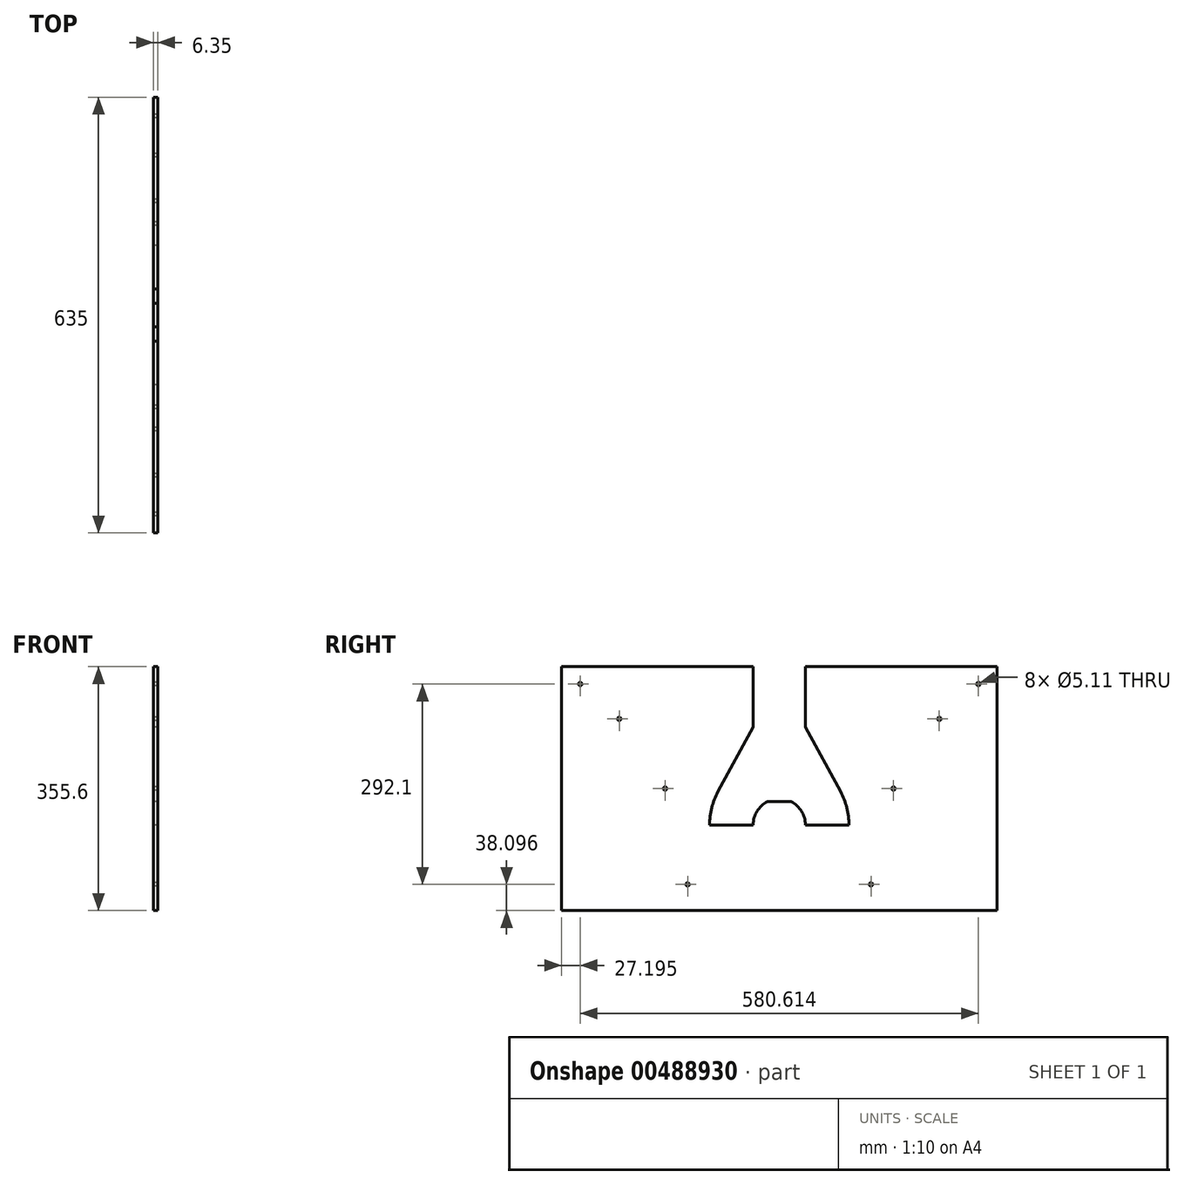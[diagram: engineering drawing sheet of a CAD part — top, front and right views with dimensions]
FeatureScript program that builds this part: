
annotation { "Feature Type Name" : "Feature", "Feature Type Description" : "" }
export const myFeature = defineFeature(function(context is Context, id is Id, definition is map)
    precondition{}
    {
        {
            var Q0;
            Q0=qCreatedBy(makeId("Right.planeOp"),FACE);
            var sketch = newSketch(context, id + "F0", { "sketchPlane" : qUnion([Q0])});
            skLineSegment(sketch, "E0.0", {"start": v(127.66, -203.13) * mm, "end": v(127.66, -196.78) * mm, "construction": true});
            skLineSegment(sketch, "E1.0", {"start": v(-507.34, -152.33) * mm, "end": v(-507.34, -145.98) * mm, "construction": true});
            skLineSegment(sketch, "E2.bottom", {"start": v(-507.34, -152.33) * mm, "end": v(127.66, -152.33) * mm});
            skLineSegment(sketch, "E2.top", {"start": v(-507.34, 203.27) * mm, "end": v(-227.94, 203.27) * mm});
            skLineSegment(sketch, "E2.left", {"start": v(-507.34, -152.33) * mm, "end": v(-507.34, 203.27) * mm});
            skLineSegment(sketch, "E2.right", {"start": v(127.66, -152.33) * mm, "end": v(127.66, 203.27) * mm});
            skLineSegment(sketch, "E3", {"start": v(-189.84, 203.27) * mm, "end": v(-189.84, -152.33) * mm, "construction": true});
            skPoint(sketch, "E4", {"position": v(-42.52, -6.28) * mm});
            skArc(sketch, "E5", {"start": v(127.66, 203.27) * mm, "mid": v(-17.26, 52.16) * mm, "end": v(-62.2, -152.33) * mm, "construction": true});
            skArc(sketch, "E6.0", {"start": v(127.66, 195.88) * mm, "mid": v(-9.58, 53) * mm, "end": v(-56.37, -139.5) * mm, "construction": true});
            skArc(sketch, "E7.0", {"start": v(99.66, 185.1) * mm, "mid": v(-22, 42.97) * mm, "end": v(-62.72, -139.65) * mm, "construction": true});
            skCircle(sketch, "E8", {"center": v(-56.16, -114.23) * mm, "radius": 2.55 * mm});
            skCircle(sketch, "E9", {"center": v(-23.27, 25.47) * mm, "radius": 2.55 * mm});
            skCircle(sketch, "E10", {"center": v(43.51, 127.07) * mm, "radius": 2.55 * mm});
            skCircle(sketch, "E11.MirrorC", {"center": v(-423.19, 127.07) * mm, "radius": 2.55 * mm});
            skCircle(sketch, "E12.MirrorC", {"center": v(-356.4, 25.47) * mm, "radius": 2.55 * mm});
            skCircle(sketch, "E13.MirrorC", {"center": v(-323.51, -114.23) * mm, "radius": 2.55 * mm});
            skLineSegment(sketch, "E14", {"start": v(-227.94, 6.42) * mm, "end": v(-151.74, 6.42) * mm});
            skLineSegment(sketch, "E15", {"start": v(-151.74, 114.93) * mm, "end": v(-151.74, 203.27) * mm});
            skLineSegment(sketch, "E16", {"start": v(-227.94, 114.93) * mm, "end": v(-227.94, 203.27) * mm});
            skPoint(sketch, "E17", {"position": v(-189.84, 6.42) * mm});
            skCircle(sketch, "E18", {"center": v(100.47, 177.87) * mm, "radius": 2.55 * mm});
            skCircle(sketch, "E19.MirrorC", {"center": v(-480.15, 177.87) * mm, "radius": 2.55 * mm});
            skLineSegment(sketch, "E20.trimOffspring", {"start": v(-151.74, 203.27) * mm, "end": v(127.66, 203.27) * mm});
            skArc(sketch, "E21", {"start": v(-88.24, -27.56) * mm, "mid": v(-91.38, -2.5) * mm, "end": v(-100.6, 21.02) * mm});
            skLineSegment(sketch, "E22", {"start": v(-291.44, -27.56) * mm, "end": v(-227.94, -27.56) * mm});
            skPoint(sketch, "E23.orphan", {"position": v(-310.29, -27.56) * mm});
            skArc(sketch, "E24", {"start": v(-151.74, -27.56) * mm, "mid": v(-189.84, 10.54) * mm, "end": v(-227.94, -27.56) * mm});
            skLineSegment(sketch, "E25.trimOffspring", {"start": v(-151.74, -27.56) * mm, "end": v(-88.24, -27.56) * mm});
            skLineSegment(sketch, "E26", {"start": v(-227.94, 114.93) * mm, "end": v(-279.07, 21.02) * mm});
            skLineSegment(sketch, "E27", {"start": v(-151.74, 114.93) * mm, "end": v(-100.6, 21.02) * mm});
            skArc(sketch, "E28.trimOffspring", {"start": v(-279.07, 21.02) * mm, "mid": v(-288.3, -2.5) * mm, "end": v(-291.44, -27.56) * mm});
            skSolve(sketch);
        }
        {
            var Q0;
            Q0=makeQuery(id+"F0.imprint","IMPRINT",FACE,{"disambiguationData":[TD([[makeQuery(id+"F0.imprint","IMPRINT",EDGE,{"derivedFrom":sQuery(id+"F0.wireOp",EDGE,"E2.bottom")}),1.0]])]});
            extrude(context, id + "F1", {"entities" : qUnion([Q0]), "depth" : 6.35 * mm, "offsetDistance" : 25.4 * mm});
        }
    });
